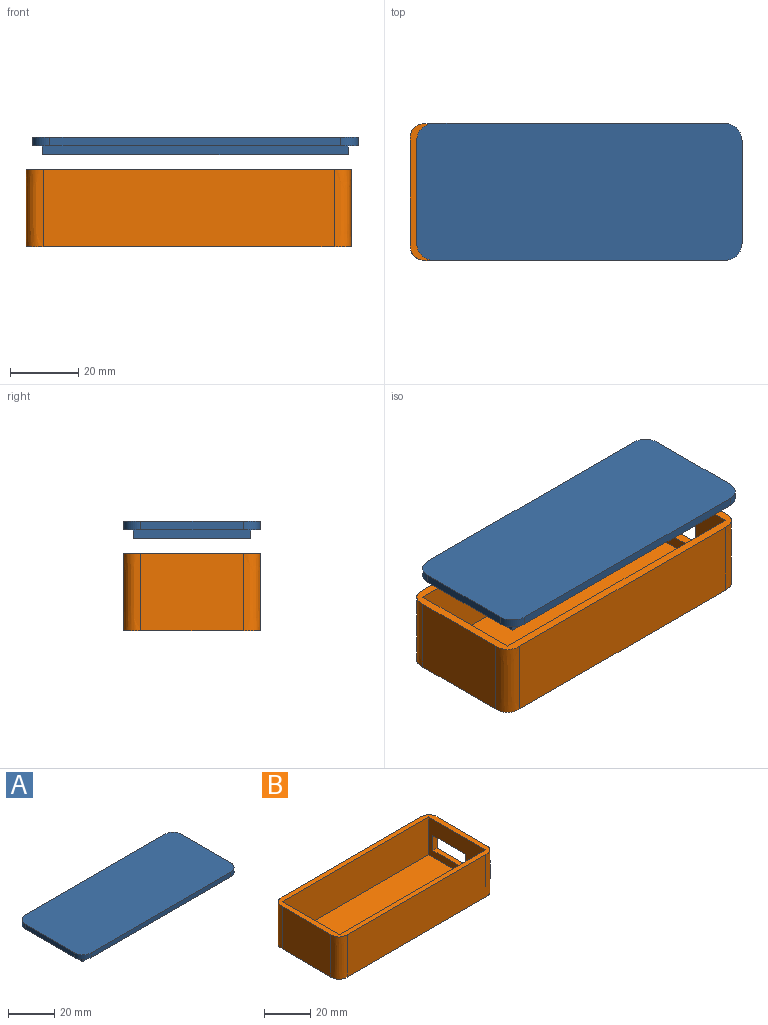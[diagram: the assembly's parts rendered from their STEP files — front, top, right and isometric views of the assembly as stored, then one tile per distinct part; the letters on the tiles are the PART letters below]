
ASSEMBLY  parts=2 mates=2
PART A: 15 faces, bbox 95x40x5 mm
  f0: plane 34.4x2.5mm, normal (-1,0,0), area 86mm2, adj f1,f3,f4,f10
  f1: plane 89.4x2.5mm, normal (0,-1,0), area 223.5mm2, adj f0,f2,f4,f10
  f2: plane 34.4x2.5mm, normal (1,0,0), area 86mm2, adj f1,f3,f4,f10
  f3: plane 89.4x2.5mm, normal (0,1,0), area 223.5mm2, adj f0,f2,f4,f10
  f4: plane 89.4x34.4mm, normal (0,0,-1), area 3075.4mm2, adj f0,f1,f2,f3
  f5: plane 30x2.5mm, normal (-1,0,0), area 75mm2, adj f9,f10,f11,f14
  f6: plane 85x2.5mm, normal (0,-1,0), area 212.5mm2, adj f9,f10,f11,f12
  f7: plane 30x2.5mm, normal (1,0,0), area 75mm2, adj f9,f10,f12,f13
  f8: plane 85x2.5mm, normal (0,1,0), area 212.5mm2, adj f9,f10,f13,f14
  f9: plane 95x40mm, normal (0,0,1), area 3778.5mm2, adj f5,f6,f7,f8,f11,f12,f13,f14
  f10: plane 95x40mm, normal (0,0,-1), area 703.2mm2, adj f0,f1,f2,f3,f5,f6,f7,f8
  f11: cylinder r=5mm len=5mm, axis (0,0,1), area 19.6mm2, adj f5,f6,f9,f10
  f12: cylinder r=5mm len=5mm, axis (0,0,-1), area 19.6mm2, adj f6,f7,f9,f10
  f13: cylinder r=5mm len=5mm, axis (0,0,1), area 19.6mm2, adj f7,f8,f9,f10
  f14: cylinder r=5mm len=5mm, axis (0,0,-1), area 19.6mm2, adj f5,f8,f9,f10
PART B: 19 faces, bbox 95.2x40.2x25 mm
  f0: plane 30x22.5mm, normal (1,0,0), area 515mm2, adj f2,f6,f12,f13,f14,f15,f17
  f1: plane 35x20mm, normal (-1,0,0), area 540mm2, adj f2,f8,f9,f10,f11,f12,f13,f14
  f2: plane 95.23x40.23mm, normal (0,0,1), area 634.5mm2, adj f0,f1,f3,f4,f5,f7,f8,f9
  f3: plane 30x22.5mm, normal (-1,0,0), area 675mm2, adj f2,f6,f16,f18
  f4: plane 85x22.5mm, normal (0,-1,0), area 1912.5mm2, adj f2,f6,f17,f18
  f5: plane 85x22.5mm, normal (0,1,0), area 1912.5mm2, adj f2,f6,f15,f16
  f6: plane 95.23x40.23mm, normal (0,0,-1), area 3784.5mm2, adj f0,f3,f4,f5,f15,f16,f17,f18
  f7: plane 35x20mm, normal (1,0,0), area 700mm2, adj f2,f8,f9,f10
  f8: plane 90x20mm, normal (0,1,0), area 1800mm2, adj f1,f2,f7,f10
  f9: plane 90x20mm, normal (0,-1,0), area 1800mm2, adj f1,f2,f7,f10
  f10: plane 90x35mm, normal (0,0,1), area 3150mm2, adj f1,f7,f8,f9
  f11: plane 8x2.5mm, normal (0,-1,0), area 20mm2, adj f1,f12,f14,f15
  f12: plane 20x2.5mm, normal (0,0,-1), area 50mm2, adj f0,f1,f11,f13
  f13: plane 8x2.5mm, normal (0,1,0), area 20mm2, adj f0,f1,f12,f14
  f14: plane 20x2.5mm, normal (0,0,1), area 50mm2, adj f0,f1,f11,f13
  f15: bspline ~22.5x5mm, area 182.9mm2, adj f0,f2,f5,f6,f11
  f16: bspline ~24.75x5mm, area 182.9mm2, adj f2,f3,f5,f6
  f17: bspline ~24.75x5mm, area 182.9mm2, adj f0,f2,f4,f6
  f18: bspline ~24.75x5mm, area 182.9mm2, adj f2,f3,f4,f6
PLACE A t=(2,0,6.9)mm
PLACE B t=(0.2,0.16,-8.68)mm fixed
MATE planar B.f5 <-> A.f8  axis (0,1,0) through (0.2,20.16,0.07)mm
MATE planar B.f4 <-> A.f6  axis (0,-1,0) through (0.2,-19.84,0.07)mm
